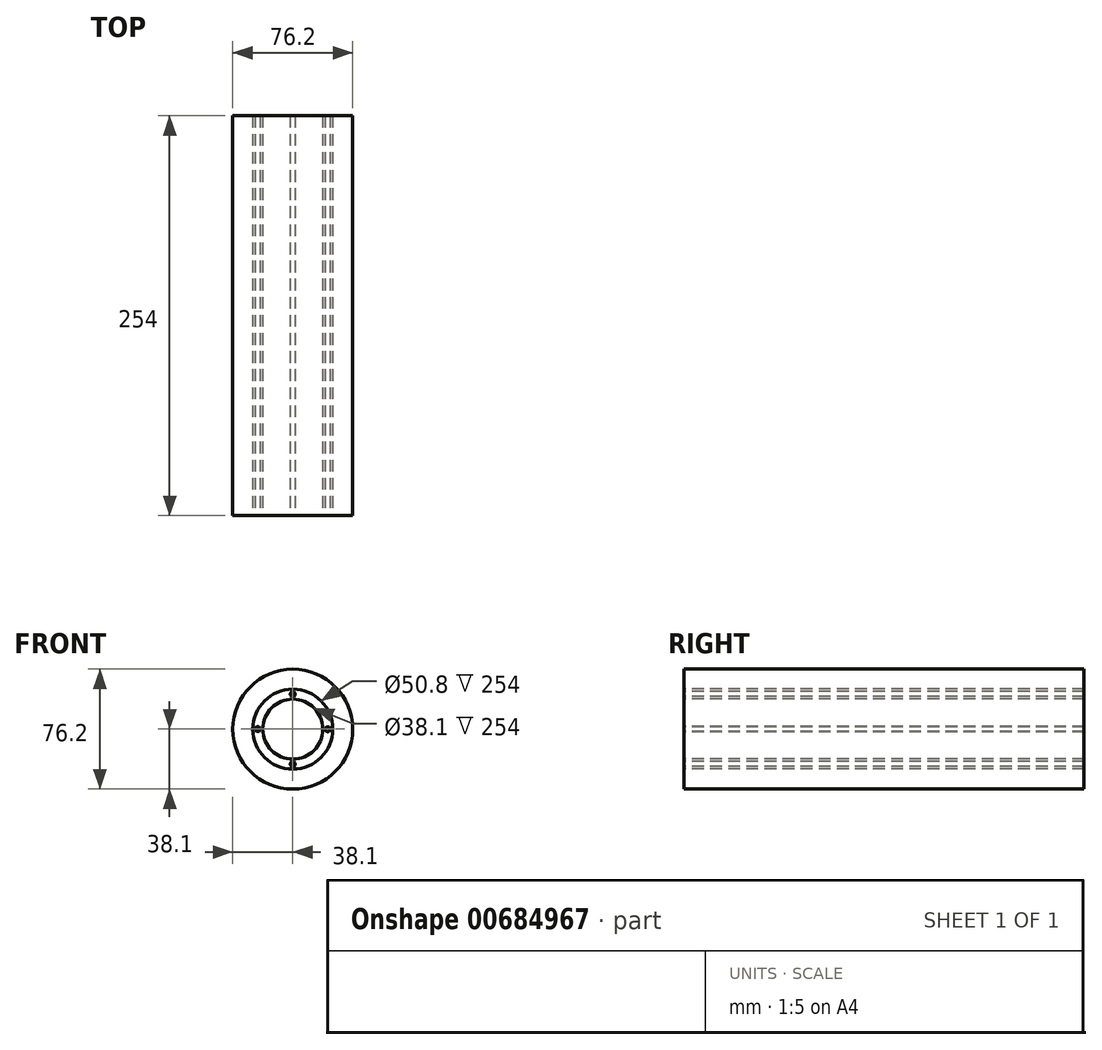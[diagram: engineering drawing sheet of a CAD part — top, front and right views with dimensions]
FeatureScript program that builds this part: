
annotation { "Feature Type Name" : "Feature", "Feature Type Description" : "" }
export const myFeature = defineFeature(function(context is Context, id is Id, definition is map)
    precondition{}
    {
        {
            var Q0;
            Q0=qCreatedBy(makeId("Front.planeOp"),FACE);
            var sketch = newSketch(context, id + "F0", { "sketchPlane" : qUnion([Q0])});
            skCircle(sketch, "E0", {"center": v(0, 0) * mm, "radius": 19.05 * mm});
            skSolve(sketch);
        }
        {
            var Q0;
            Q0=qCreatedBy(makeId("Front.planeOp"),FACE);
            var sketch = newSketch(context, id + "F1", { "sketchPlane" : qUnion([Q0])});
            skCircle(sketch, "E1", {"center": v(0, 0) * mm, "radius": 25.4 * mm});
            skCircle(sketch, "E2.0", {"center": v(0, 0) * mm, "radius": 19.05 * mm});
            skSolve(sketch);
        }
        {
            var Q0;
            Q0=qCreatedBy(makeId("Front.planeOp"),FACE);
            var sketch = newSketch(context, id + "F2", { "sketchPlane" : qUnion([Q0])});
            skCircle(sketch, "E3", {"center": v(0, 0) * mm, "radius": 38.1 * mm});
            skCircle(sketch, "E4.0", {"center": v(0, 0) * mm, "radius": 25.4 * mm});
            skSolve(sketch);
        }
        {
            var Q0;
            Q0=qCreatedBy(makeId("Front.planeOp"),FACE);
            var sketch = newSketch(context, id + "F3", { "sketchPlane" : qUnion([Q0])});
            skCircle(sketch, "E5", {"center": v(0, 22.23) * mm, "radius": 1.59 * mm});
            skCircle(sketch, "E6", {"center": v(-22.23, 0) * mm, "radius": 1.59 * mm});
            skCircle(sketch, "E7", {"center": v(22.22, -0.04) * mm, "radius": 1.59 * mm});
            skCircle(sketch, "E8", {"center": v(0, -22.23) * mm, "radius": 1.59 * mm});
            skSolve(sketch);
        }
        {
            var Q0;
            Q0=qSketchRegion(id+"F2",true);
            extrude(context, id + "F4", {"entities" : qUnion([Q0]), "oppositeDirection" : true, "depth" : 254 * mm});
        }
        {
            var Q0;
            Q0=qSketchRegion(id+"F1",true);
            extrude(context, id + "F5", {"entities" : qUnion([Q0]), "oppositeDirection" : true, "depth" : 254 * mm});
        }
        {
            var Q0;
            Q0=qSketchRegion(id+"F0",true);
            extrude(context, id + "F6", {"entities" : qUnion([Q0]), "oppositeDirection" : true, "depth" : 254 * mm, "hasSecondDirection" : true, "secondDirectionOppositeDirection" : true, "secondDirectionDepth" : 25.4 * mm});
        }
        {
            var Q0;
            Q0=qSketchRegion(id+"F3",true);
            extrude(context, id + "F7", {"entities" : qUnion([Q0]), "oppositeDirection" : true, "depth" : 254 * mm});
        }
        {
            var Q0;
            Q0=qSketchRegion(id+"F0",true);
            extrude(context, id + "F8", {"entities" : qUnion([Q0]), "oppositeDirection" : true, "depth" : 254 * mm});
        }
        {
            var Q0;
            Q0=makeQuery(id+"F6.opExtrude","SWEPT_BODY",BODY,{"disambiguationData":[OSD([sQuery(id+"F0.wireOp",EDGE,"E0")])]});
            deleteBodies(context, id + "F9", {"entities" : qUnion([Q0])});
        }
        {
            var Q0;
            Q0=makeQuery(id+"F7.opExtrude","SWEPT_BODY",BODY,{"disambiguationData":[OSD([sQuery(id+"F3.wireOp",EDGE,"E6")])]});
            transform(context, id + "F10", {"entities" : qUnion([Q0]), "transformType" : TransformType.TRANSLATION_3D, "dx" : 0 * mm, "dy" : 0 * mm, "dz" : 0 * mm, "makeCopy" : true});
        }
        {
            var Q0;
            Q0=makeQuery(id+"F10.opPattern","COPY",BODY,{"derivedFrom":makeQuery(id+"F7.opExtrude","SWEPT_BODY",BODY,{"disambiguationData":[OSD([sQuery(id+"F3.wireOp",EDGE,"E6")])]}),"instanceName":"1"});
            deleteBodies(context, id + "F11", {"entities" : qUnion([Q0])});
        }
        {
            var Q0;
            Q0=qSketchRegion(id+"F0",true);
            extrude(context, id + "F12", {"entities" : qUnion([Q0]), "oppositeDirection" : true, "depth" : 254 * mm});
        }
    });
